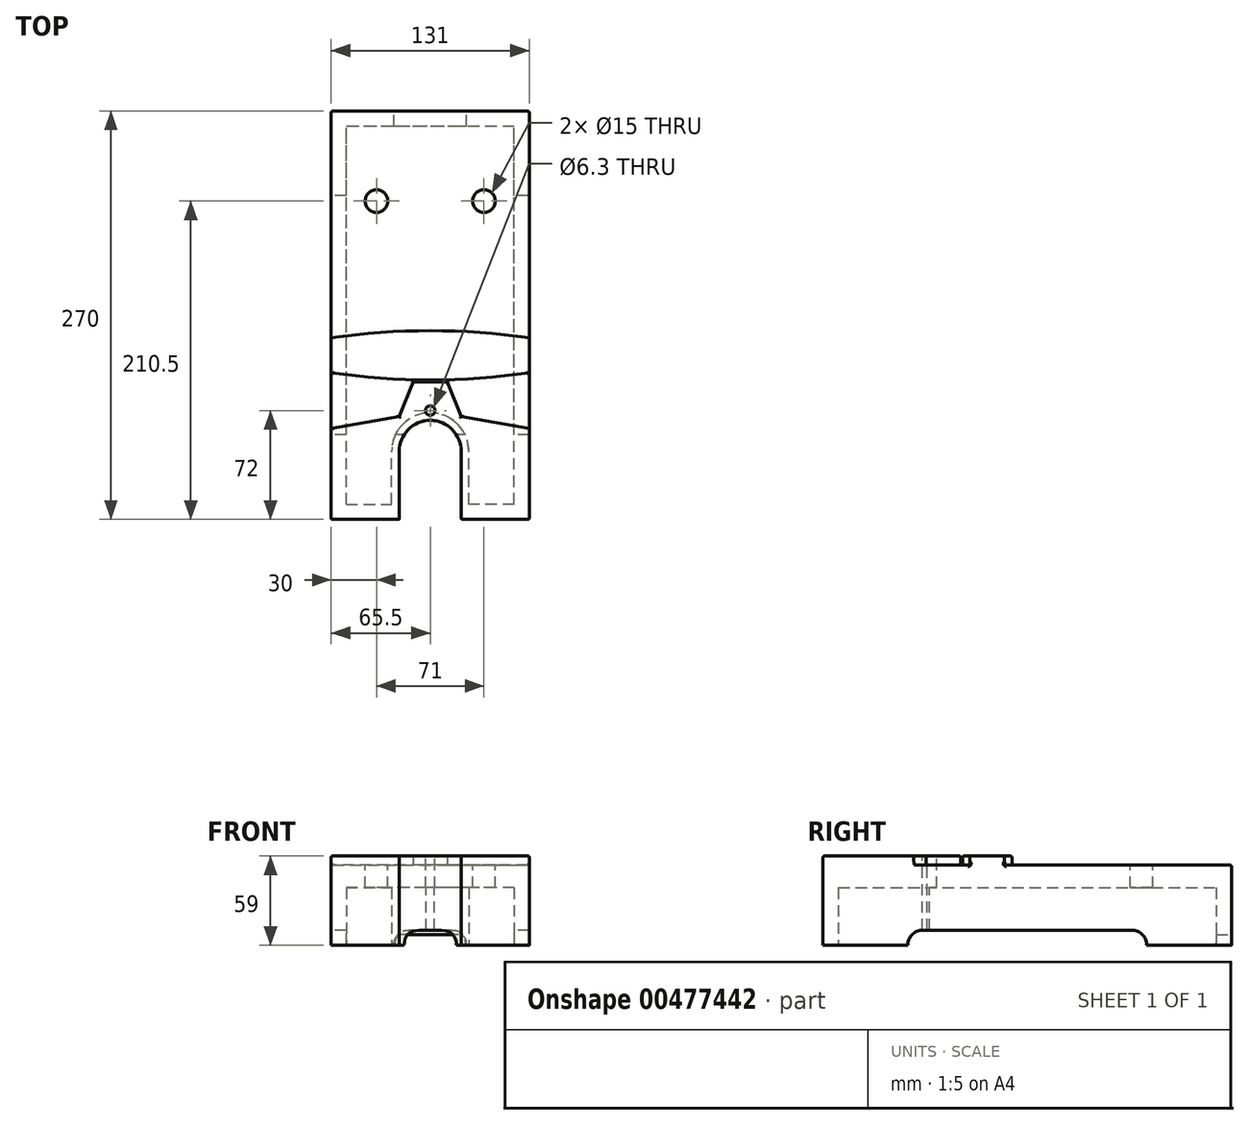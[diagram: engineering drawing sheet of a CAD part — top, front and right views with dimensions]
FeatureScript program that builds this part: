
annotation { "Feature Type Name" : "Feature", "Feature Type Description" : "" }
export const myFeature = defineFeature(function(context is Context, id is Id, definition is map)
    precondition{}
    {
        {
            var Q0;
            Q0=qCreatedBy(makeId("Top.planeOp"),FACE);
            var sketch = newSketch(context, id + "F0", { "sketchPlane" : qUnion([Q0])});
            skLineSegment(sketch, "E0.bottom", {"start": v(-65.5, 135) * mm, "end": v(65.5, 135) * mm});
            skLineSegment(sketch, "E0.top", {"start": v(-65.5, -135) * mm, "end": v(65.5, -135) * mm});
            skLineSegment(sketch, "E0.left", {"start": v(-65.5, 135) * mm, "end": v(-65.5, -135) * mm});
            skLineSegment(sketch, "E0.right", {"start": v(65.5, 135) * mm, "end": v(65.5, -135) * mm});
            skSolve(sketch);
        }
        {
            var Q0;
            Q0=makeQuery(id+"F0.imprint","IMPRINT",FACE,{"disambiguationData":[TD([[makeQuery(id+"F0.imprint","IMPRINT",EDGE,{"derivedFrom":sQuery(id+"F0.wireOp",EDGE,"E0.bottom")}),-1.0]])]});
            extrude(context, id + "F1", {"entities" : qUnion([Q0]), "depth" : 53 * mm});
        }
        {
            var Q0;
            Q0=makeQuery(id+"F1.opExtrude","CAP_FACE",FACE,{"disambiguationData":[OSD([sQuery(id+"F0.wireOp",EDGE,"E0.bottom"),sQuery(id+"F0.wireOp",EDGE,"E0.top"),sQuery(id+"F0.wireOp",EDGE,"E0.left"),sQuery(id+"F0.wireOp",EDGE,"E0.right")])],"isStart":true});
            var sketch = newSketch(context, id + "F2", { "sketchPlane" : qUnion([Q0])});
            skLineSegment(sketch, "E1.bottom", {"start": v(65.5, -79) * mm, "end": v(-65.5, -79) * mm});
            skLineSegment(sketch, "E1.top", {"start": v(65.5, 79) * mm, "end": v(-65.5, 79) * mm});
            skLineSegment(sketch, "E1.left", {"start": v(65.5, -79) * mm, "end": v(65.5, 79) * mm});
            skLineSegment(sketch, "E1.right", {"start": v(-65.5, -79) * mm, "end": v(-65.5, 79) * mm});
            skSolve(sketch);
        }
        {
            var Q0;
            Q0 = qSketchRegion(id + "F2", true);
            extrude(context, id + "F3", {"entities" : qUnion([Q0]), "operationType" : NewBodyOperationType.REMOVE, "oppositeDirection" : true, "depth" : 10 * mm});
        }
        {
            var Q0;
            Q0=makeQuery(id+"F3.boolean.opBoolean","COPY",EDGE,{"derivedFrom":makeQuery(id+"F3.opExtrude","CAP_EDGE",EDGE,{"disambiguationData":[OSD([sQuery(id+"F2.wireOp",EDGE,"E1.top")])],"isStart":false})});
            var Q1;
            Q1=makeQuery(id+"F3.boolean.opBoolean","COPY",EDGE,{"derivedFrom":makeQuery(id+"F3.opExtrude","CAP_EDGE",EDGE,{"disambiguationData":[OSD([sQuery(id+"F2.wireOp",EDGE,"E1.bottom")])],"isStart":false})});
            fillet(context, id + "F4", {"entities" : qUnion([Q0, Q1]), "radius" : 10 * mm, "tangentPropagation" : true, "allowEdgeOverflow" : false});
        }
        {
            var Q0;
            Q0=makeQuery(id+"F1.opExtrude","CAP_FACE",FACE,{"disambiguationData":[OSD([sQuery(id+"F0.wireOp",EDGE,"E0.bottom"),sQuery(id+"F0.wireOp",EDGE,"E0.top"),sQuery(id+"F0.wireOp",EDGE,"E0.left"),sQuery(id+"F0.wireOp",EDGE,"E0.right")])],"isStart":false});
            var sketch = newSketch(context, id + "F5", { "sketchPlane" : qUnion([Q0])});
            skLineSegment(sketch, "E2", {"start": v(-65.5, -135) * mm, "end": v(-65.5, -75) * mm});
            skLineSegment(sketch, "E3", {"start": v(-65.5, -75) * mm, "end": v(-20.5, -67) * mm});
            skLineSegment(sketch, "E4", {"start": v(-20.5, -67) * mm, "end": v(-11.2, -44.07) * mm});
            skLineSegment(sketch, "E5", {"start": v(-11.2, -44.07) * mm, "end": v(0, -44.07) * mm});
            skLineSegment(sketch, "E6", {"start": v(-65.5, -75) * mm, "end": v(-65.5, -135) * mm});
            skLineSegment(sketch, "E7.MirrorCS", {"start": v(11.2, -44.07) * mm, "end": v(0, -44.07) * mm});
            skLineSegment(sketch, "E8.MirrorCS", {"start": v(20.5, -67) * mm, "end": v(11.2, -44.07) * mm});
            skLineSegment(sketch, "E9.MirrorCS", {"start": v(65.5, -75) * mm, "end": v(20.5, -67) * mm});
            skLineSegment(sketch, "E10.MirrorCS", {"start": v(65.5, -75) * mm, "end": v(65.5, -135) * mm});
            skLineSegment(sketch, "E11", {"start": v(-65.5, -135) * mm, "end": v(0, -135) * mm});
            skLineSegment(sketch, "E12.MirrorCS", {"start": v(65.5, -135) * mm, "end": v(0, -135) * mm});
            skSolve(sketch);
        }
        {
            var Q0;
            Q0 = qSketchRegion(id + "F5", true);
            extrude(context, id + "F6", {"entities" : qUnion([Q0]), "operationType" : NewBodyOperationType.ADD, "depth" : 6 * mm});
        }
        {
            var Q0;
            Q0=makeQuery(id+"F6.opExtrude","CAP_FACE",FACE,{"disambiguationData":[OSD([sQuery(id+"F5.wireOp",EDGE,"E3"),sQuery(id+"F5.wireOp",EDGE,"E4"),sQuery(id+"F5.wireOp",EDGE,"E5"),sQuery(id+"F5.wireOp",EDGE,"E6"),sQuery(id+"F5.wireOp",EDGE,"E7.MirrorCS"),sQuery(id+"F5.wireOp",EDGE,"E8.MirrorCS"),sQuery(id+"F5.wireOp",EDGE,"E9.MirrorCS"),sQuery(id+"F5.wireOp",EDGE,"E10.MirrorCS"),sQuery(id+"F5.wireOp",EDGE,"E11"),sQuery(id+"F5.wireOp",EDGE,"E12.MirrorCS")])],"isStart":false});
            var sketch = newSketch(context, id + "F7", { "sketchPlane" : qUnion([Q0])});
            skLineSegment(sketch, "E13.top", {"start": v(-20.5, -135) * mm, "end": v(20.5, -135) * mm});
            skLineSegment(sketch, "E13.left", {"start": v(-20.5, -90) * mm, "end": v(-20.5, -135) * mm});
            skLineSegment(sketch, "E13.right", {"start": v(20.5, -90) * mm, "end": v(20.5, -135) * mm});
            skArc(sketch, "E14", {"start": v(-20.5, -90) * mm, "mid": v(0, -69.5) * mm, "end": v(20.5, -90) * mm});
            skSolve(sketch);
        }
        {
            var Q0;
            Q0 = qSketchRegion(id + "F7", true);
            extrude(context, id + "F8", {"entities" : qUnion([Q0]), "operationType" : NewBodyOperationType.REMOVE, "oppositeDirection" : true, "depth" : 63.1 * mm});
        }
        {
            var Q0;
            Q0=makeQuery(id+"F1.opExtrude","CAP_FACE",FACE,{"disambiguationData":[OSD([sQuery(id+"F0.wireOp",EDGE,"E0.bottom"),sQuery(id+"F0.wireOp",EDGE,"E0.top"),sQuery(id+"F0.wireOp",EDGE,"E0.left"),sQuery(id+"F0.wireOp",EDGE,"E0.right")])],"isStart":false});
            var sketch = newSketch(context, id + "F9", { "sketchPlane" : qUnion([Q0])});
            skLineSegment(sketch, "E15", {"start": v(-65.5, -15) * mm, "end": v(-65.5, -38) * mm});
            skLineSegment(sketch, "E16.MirrorCS", {"start": v(65.5, -15) * mm, "end": v(65.5, -38) * mm});
            skArc(sketch, "E17", {"start": v(-65.5, -38) * mm, "mid": v(0, -42.8) * mm, "end": v(65.5, -38) * mm});
            skArc(sketch, "E18", {"start": v(-65.5, -15) * mm, "mid": v(0, -10.2) * mm, "end": v(65.5, -15) * mm});
            skSolve(sketch);
        }
        {
            var Q0;
            Q0 = qSketchRegion(id + "F9", true);
            extrude(context, id + "F10", {"entities" : qUnion([Q0]), "operationType" : NewBodyOperationType.ADD, "depth" : 6 * mm});
        }
        {
            var Q0;
            Q0=qCreatedBy(makeId("Top.planeOp"),FACE);
            var sketch = newSketch(context, id + "F11", { "sketchPlane" : qUnion([Q0])});
            skLineSegment(sketch, "E19", {"start": v(-55.5, -125) * mm, "end": v(-55.5, 125) * mm});
            skLineSegment(sketch, "E20", {"start": v(-55.5, 125) * mm, "end": v(0, 125) * mm});
            skLineSegment(sketch, "E21", {"start": v(-55.5, -125) * mm, "end": v(-25.5, -125) * mm});
            skLineSegment(sketch, "E22", {"start": v(-25.5, -125) * mm, "end": v(-25.5, -90) * mm});
            skLineSegment(sketch, "E23", {"start": v(-25.5, -90) * mm, "end": v(25.5, -90) * mm, "construction": true});
            skArc(sketch, "E24", {"start": v(-25.5, -90) * mm, "mid": v(-18.03, -71.97) * mm, "end": v(0, -64.5) * mm});
            skLineSegment(sketch, "E25.MirrorCS", {"start": v(55.5, 125) * mm, "end": v(0, 125) * mm});
            skLineSegment(sketch, "E26.MirrorCS", {"start": v(55.5, -125) * mm, "end": v(55.5, 125) * mm});
            skLineSegment(sketch, "E27.MirrorCS", {"start": v(55.5, -125) * mm, "end": v(25.5, -125) * mm});
            skLineSegment(sketch, "E28.MirrorCS", {"start": v(25.5, -125) * mm, "end": v(25.5, -90) * mm});
            skArc(sketch, "E29.MirrorCS", {"start": v(25.5, -90) * mm, "mid": v(18.03, -71.97) * mm, "end": v(0, -64.5) * mm});
            skSolve(sketch);
        }
        {
            var Q0;
            Q0 = qSketchRegion(id + "F11", true);
            extrude(context, id + "F12", {"entities" : qUnion([Q0]), "operationType" : NewBodyOperationType.REMOVE, "depth" : 38 * mm});
        }
        {
            var Q0;
            Q0=makeQuery(id+"F1.opExtrude","SWEPT_FACE",FACE,{"disambiguationData":[OSD([sQuery(id+"F0.wireOp",EDGE,"E0.bottom")])]});
            var sketch = newSketch(context, id + "F13", { "sketchPlane" : qUnion([Q0])});
            skLineSegment(sketch, "E30.bottom", {"start": v(-24, 0) * mm, "end": v(24, 0) * mm});
            skLineSegment(sketch, "E30.top", {"start": v(-24, 7) * mm, "end": v(24, 7) * mm});
            skLineSegment(sketch, "E30.left", {"start": v(-24, 0) * mm, "end": v(-24, 7) * mm});
            skLineSegment(sketch, "E30.right", {"start": v(24, 0) * mm, "end": v(24, 7) * mm});
            skSolve(sketch);
        }
        {
            var Q0;
            Q0 = qSketchRegion(id + "F13", true);
            extrude(context, id + "F14", {"entities" : qUnion([Q0]), "operationType" : NewBodyOperationType.REMOVE, "oppositeDirection" : true, "depth" : 10 * mm});
        }
        {
            var Q0;
            Q0=makeQuery(id+"F14.boolean.opBoolean","COPY",EDGE,{"derivedFrom":makeQuery(id+"F14.opExtrude","SWEPT_EDGE",EDGE,{"disambiguationData":[OSD([sQuery(id+"F13.wireOp",EDGE,"E30.top"),sQuery(id+"F13.wireOp",EDGE,"E30.right")])]})});
            var Q1;
            Q1=makeQuery(id+"F14.boolean.opBoolean","COPY",EDGE,{"derivedFrom":makeQuery(id+"F14.opExtrude","SWEPT_EDGE",EDGE,{"disambiguationData":[OSD([sQuery(id+"F13.wireOp",EDGE,"E30.top"),sQuery(id+"F13.wireOp",EDGE,"E30.left")])]})});
            fillet(context, id + "F15", {"entities" : qUnion([Q0, Q1]), "radius" : 5 * mm, "tangentPropagation" : true, "allowEdgeOverflow" : false});
        }
        {
            var Q0;
            {var subQ0=sQuery(id+"F0.wireOp",EDGE,"E0.left");var subQ1=sQuery(id+"F0.wireOp",EDGE,"E0.right");var subQ2=sQuery(id+"F0.wireOp",EDGE,"E0.bottom");Q0=makeQuery(id+"F10.boolean.opBoolean","SPLIT",FACE,{"disambiguationData":[TD([makeQuery(id+"F1.opExtrude","SWEPT_FACE",FACE,{"disambiguationData":[OSD([subQ2])]})])],"derivedFrom":makeQuery(id+"F1.opExtrude","CAP_FACE",FACE,{"disambiguationData":[OSD([subQ2,sQuery(id+"F0.wireOp",EDGE,"E0.top"),subQ0,subQ1])],"isStart":false})});}
            var sketch = newSketch(context, id + "F16", { "sketchPlane" : qUnion([Q0])});
            skPoint(sketch, "E31", {"position": v(-35.5, 75.5) * mm});
            skPoint(sketch, "E32.MirrorP", {"position": v(35.5, 75.5) * mm});
            skSolve(sketch);
        }
        {
            var Q0;
            Q0=sQuery(id+"F16.wireOp",VERTEX,"E31");
            var Q1;
            Q1=sQuery(id+"F16.wireOp",VERTEX,"E32.MirrorP");
            var Q2;
            Q2=makeQuery(id+"F1.opExtrude","SWEPT_BODY",BODY,{"disambiguationData":[OSD([sQuery(id+"F0.wireOp",EDGE,"E0.bottom"),sQuery(id+"F0.wireOp",EDGE,"E0.top"),sQuery(id+"F0.wireOp",EDGE,"E0.left"),sQuery(id+"F0.wireOp",EDGE,"E0.right")])]});
            hole(context, id + "F17", {"style" : HoleStyle.SIMPLE, "endStyle" : HoleEndStyle.THROUGH, "holeDiameter" : 15 * mm, "isTappedThrough" : true, "tappedDepth" : 12 * mm, "tapClearance" : 3, "locations" : qUnion([Q0, Q1]), "scope" : qUnion([Q2])});
        }
        {
            var Q0;
            Q0=makeQuery(id+"F6.opExtrude","CAP_FACE",FACE,{"disambiguationData":[OSD([sQuery(id+"F5.wireOp",EDGE,"E3"),sQuery(id+"F5.wireOp",EDGE,"E4"),sQuery(id+"F5.wireOp",EDGE,"E5"),sQuery(id+"F5.wireOp",EDGE,"E6"),sQuery(id+"F5.wireOp",EDGE,"E7.MirrorCS"),sQuery(id+"F5.wireOp",EDGE,"E8.MirrorCS"),sQuery(id+"F5.wireOp",EDGE,"E9.MirrorCS"),sQuery(id+"F5.wireOp",EDGE,"E10.MirrorCS"),sQuery(id+"F5.wireOp",EDGE,"E11"),sQuery(id+"F5.wireOp",EDGE,"E12.MirrorCS")])],"isStart":false});
            var sketch = newSketch(context, id + "F18", { "sketchPlane" : qUnion([Q0])});
            skPoint(sketch, "E33", {"position": v(0, -63) * mm});
            skSolve(sketch);
        }
        {
            var Q0;
            Q0=sQuery(id+"F18.wireOp",VERTEX,"E33");
            var Q1;
            Q1=makeQuery(id+"F1.opExtrude","SWEPT_BODY",BODY,{"disambiguationData":[OSD([sQuery(id+"F0.wireOp",EDGE,"E0.bottom"),sQuery(id+"F0.wireOp",EDGE,"E0.top"),sQuery(id+"F0.wireOp",EDGE,"E0.left"),sQuery(id+"F0.wireOp",EDGE,"E0.right")])]});
            hole(context, id + "F19", {"style" : HoleStyle.SIMPLE, "endStyle" : HoleEndStyle.THROUGH, "holeDiameter" : 6.3 * mm, "isTappedThrough" : true, "tappedDepth" : 12 * mm, "tapClearance" : 3, "locations" : qUnion([Q0]), "scope" : qUnion([Q1])});
        }
        {
            var Q0;
            {var subQ0=sQuery(id+"F0.wireOp",EDGE,"E0.left");var subQ1=sQuery(id+"F0.wireOp",EDGE,"E0.right");var subQ2=sQuery(id+"F0.wireOp",EDGE,"E0.bottom");Q0=makeQuery(id+"F10.boolean.opBoolean","SPLIT",FACE,{"disambiguationData":[TD([makeQuery(id+"F1.opExtrude","SWEPT_FACE",FACE,{"disambiguationData":[OSD([subQ2])]})])],"derivedFrom":makeQuery(id+"F1.opExtrude","CAP_FACE",FACE,{"disambiguationData":[OSD([subQ2,sQuery(id+"F0.wireOp",EDGE,"E0.top"),subQ0,subQ1])],"isStart":false})});}
            var Q1;
            Q1=makeQuery(id+"F10.opExtrude","CAP_FACE",FACE,{"disambiguationData":[OSD([sQuery(id+"F9.wireOp",EDGE,"E15"),sQuery(id+"F9.wireOp",EDGE,"E16.MirrorCS"),sQuery(id+"F9.wireOp",EDGE,"E17"),sQuery(id+"F9.wireOp",EDGE,"E18")])],"isStart":false});
            var Q2;
            Q2=makeQuery(id+"F6.opExtrude","CAP_FACE",FACE,{"disambiguationData":[OSD([sQuery(id+"F5.wireOp",EDGE,"E3"),sQuery(id+"F5.wireOp",EDGE,"E4"),sQuery(id+"F5.wireOp",EDGE,"E5"),sQuery(id+"F5.wireOp",EDGE,"E6"),sQuery(id+"F5.wireOp",EDGE,"E7.MirrorCS"),sQuery(id+"F5.wireOp",EDGE,"E8.MirrorCS"),sQuery(id+"F5.wireOp",EDGE,"E9.MirrorCS"),sQuery(id+"F5.wireOp",EDGE,"E10.MirrorCS"),sQuery(id+"F5.wireOp",EDGE,"E11"),sQuery(id+"F5.wireOp",EDGE,"E12.MirrorCS")])],"isStart":false});
            var Q3;
            {var subQ0=sQuery(id+"F0.wireOp",EDGE,"E0.left");var subQ1=sQuery(id+"F0.wireOp",EDGE,"E0.right");Q3=makeQuery(id+"F10.boolean.opBoolean","SPLIT",FACE,{"disambiguationData":[TD([makeQuery(id+"F6.opExtrude","SWEPT_FACE",FACE,{"disambiguationData":[OSD([sQuery(id+"F5.wireOp",EDGE,"E3")])]})])],"derivedFrom":makeQuery(id+"F1.opExtrude","CAP_FACE",FACE,{"disambiguationData":[OSD([sQuery(id+"F0.wireOp",EDGE,"E0.bottom"),sQuery(id+"F0.wireOp",EDGE,"E0.top"),subQ0,subQ1])],"isStart":false})});}
            var Q4;
            Q4=makeQuery(id+"F6.boolean.opBoolean","MERGE",EDGE,{"derivedFrom":[makeQuery(id+"F1.opExtrude","SWEPT_EDGE",EDGE,{"disambiguationData":[OSD([sQuery(id+"F0.wireOp",EDGE,"E0.top"),sQuery(id+"F0.wireOp",EDGE,"E0.left")])]}),makeQuery(id+"F6.opExtrude","SWEPT_EDGE",EDGE,{"disambiguationData":[OSD([sQuery(id+"F5.wireOp",EDGE,"E6"),sQuery(id+"F5.wireOp",EDGE,"E11")])]})]});
            var Q5;
            Q5=makeQuery(id+"F8.boolean.opBoolean","COPY",EDGE,{"derivedFrom":makeQuery(id+"F8.opExtrude","SWEPT_EDGE",EDGE,{"disambiguationData":[OSD([sQuery(id+"F5.wireOp",EDGE,"E11"),sQuery(id+"F5.wireOp",EDGE,"E12.MirrorCS"),sQuery(id+"F7.wireOp",EDGE,"E13.top"),sQuery(id+"F7.wireOp",EDGE,"E13.left")])]})});
            var Q6;
            Q6=makeQuery(id+"F8.boolean.opBoolean","COPY",EDGE,{"derivedFrom":makeQuery(id+"F8.opExtrude","SWEPT_EDGE",EDGE,{"disambiguationData":[OSD([sQuery(id+"F5.wireOp",EDGE,"E11"),sQuery(id+"F5.wireOp",EDGE,"E12.MirrorCS"),sQuery(id+"F7.wireOp",EDGE,"E13.top"),sQuery(id+"F7.wireOp",EDGE,"E13.right")])]})});
            var Q7;
            Q7=makeQuery(id+"F6.boolean.opBoolean","MERGE",EDGE,{"derivedFrom":[makeQuery(id+"F1.opExtrude","SWEPT_EDGE",EDGE,{"disambiguationData":[OSD([sQuery(id+"F0.wireOp",EDGE,"E0.top"),sQuery(id+"F0.wireOp",EDGE,"E0.right")])]}),makeQuery(id+"F6.opExtrude","SWEPT_EDGE",EDGE,{"disambiguationData":[OSD([sQuery(id+"F5.wireOp",EDGE,"E10.MirrorCS"),sQuery(id+"F5.wireOp",EDGE,"E12.MirrorCS")])]})]});
            var Q8;
            Q8=makeQuery(id+"F1.opExtrude","SWEPT_EDGE",EDGE,{"disambiguationData":[OSD([sQuery(id+"F0.wireOp",EDGE,"E0.bottom"),sQuery(id+"F0.wireOp",EDGE,"E0.right")])]});
            var Q9;
            Q9=makeQuery(id+"F1.opExtrude","SWEPT_EDGE",EDGE,{"disambiguationData":[OSD([sQuery(id+"F0.wireOp",EDGE,"E0.bottom"),sQuery(id+"F0.wireOp",EDGE,"E0.left")])]});
            fillet(context, id + "F20", {"entities" : qUnion([Q0, Q1, Q2, Q3, Q4, Q5, Q6, Q7, Q8, Q9]), "radius" : 1 * mm, "tangentPropagation" : true, "allowEdgeOverflow" : false});
        }
    });
